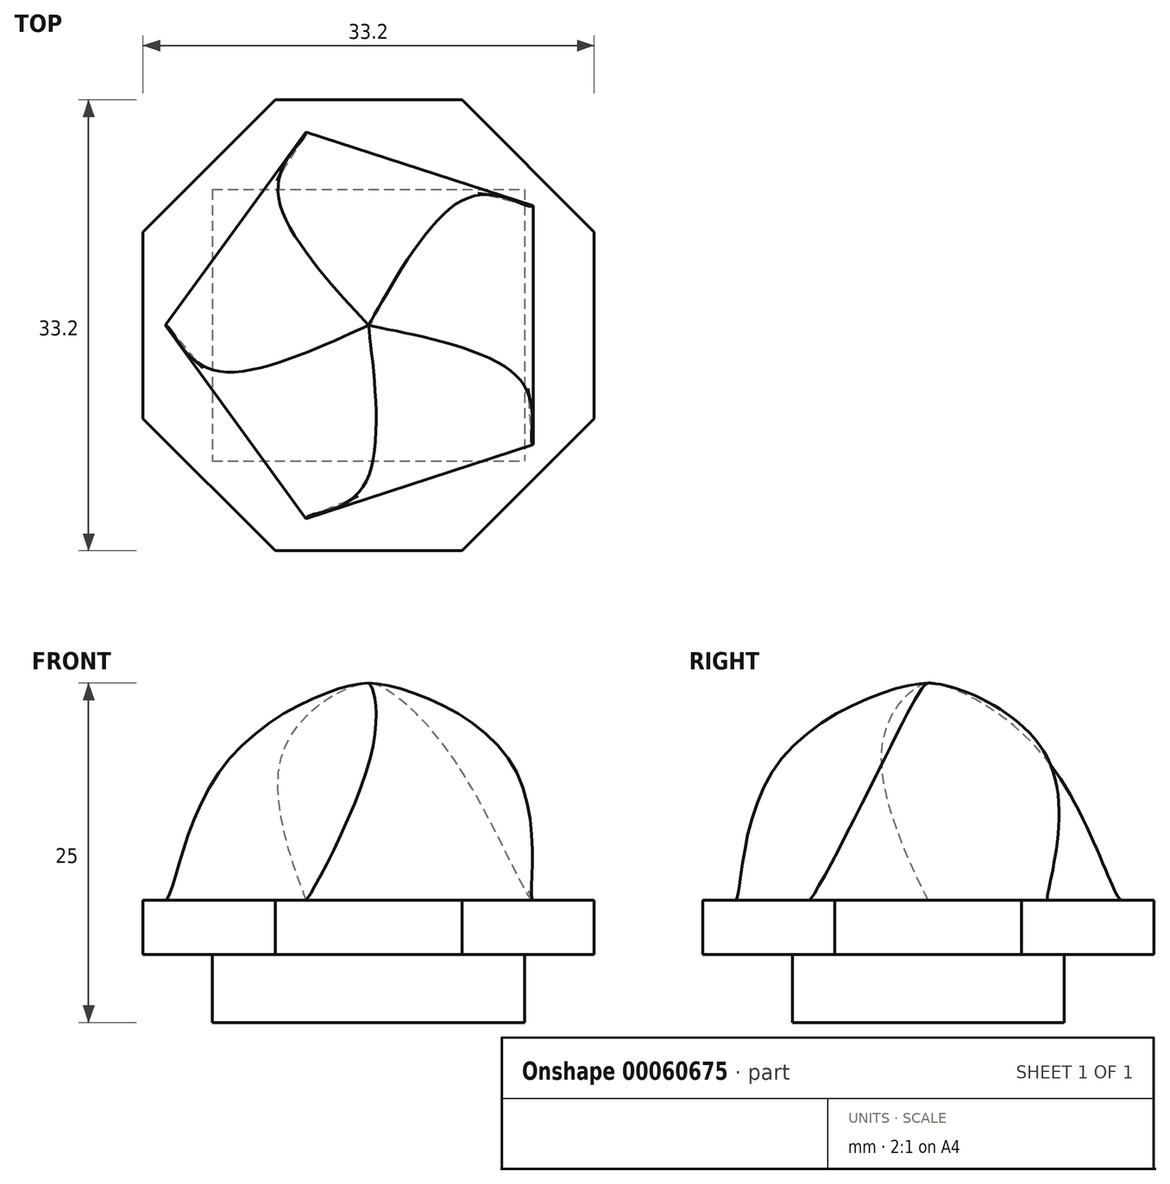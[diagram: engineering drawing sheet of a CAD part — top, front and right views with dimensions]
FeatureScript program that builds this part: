
annotation { "Feature Type Name" : "Feature", "Feature Type Description" : "" }
export const myFeature = defineFeature(function(context is Context, id is Id, definition is map)
    precondition{}
    {
        {
            var Q0;
            Q0=qCreatedBy(makeId("Top.planeOp"),FACE);
            var sketch = newSketch(context, id + "F0", { "sketchPlane" : qUnion([Q0])});
            skLineSegment(sketch, "E0.bottom", {"start": v(-11.5, 10) * mm, "end": v(11.5, 10) * mm});
            skLineSegment(sketch, "E0.top", {"start": v(-11.5, -10) * mm, "end": v(11.5, -10) * mm});
            skLineSegment(sketch, "E0.left", {"start": v(-11.5, 10) * mm, "end": v(-11.5, -10) * mm});
            skLineSegment(sketch, "E0.right", {"start": v(11.5, 10) * mm, "end": v(11.5, -10) * mm});
            skSolve(sketch);
        }
        {
            var Q0;
            Q0=qSketchRegion(id+"F0",true);
            extrude(context, id + "F1", {"entities" : qUnion([Q0]), "depth" : 5 * mm});
        }
        {
            var Q0;
            Q0=makeQuery(id+"F1.opExtrude","CAP_FACE",FACE,{"disambiguationData":[OSD([sQuery(id+"F0.wireOp",EDGE,"E0.bottom"),sQuery(id+"F0.wireOp",EDGE,"E0.top"),sQuery(id+"F0.wireOp",EDGE,"E0.left"),sQuery(id+"F0.wireOp",EDGE,"E0.right")])],"isStart":false});
            var sketch = newSketch(context, id + "F2", { "sketchPlane" : qUnion([Q0])});
            skCircle(sketch, "E1.cCircle", {"center": v(0, 0) * mm, "radius": 16.6 * mm, "construction": true});
            skLineSegment(sketch, "E1.0", {"start": v(16.6, 6.88) * mm, "end": v(16.6, -6.88) * mm});
            skLineSegment(sketch, "E1.1", {"start": v(16.6, -6.88) * mm, "end": v(6.88, -16.6) * mm});
            skLineSegment(sketch, "E1.2", {"start": v(6.88, -16.6) * mm, "end": v(-6.88, -16.6) * mm});
            skLineSegment(sketch, "E1.3", {"start": v(-6.88, -16.6) * mm, "end": v(-16.6, -6.88) * mm});
            skLineSegment(sketch, "E1.4", {"start": v(-16.6, -6.88) * mm, "end": v(-16.6, 6.88) * mm});
            skLineSegment(sketch, "E1.5", {"start": v(-16.6, 6.88) * mm, "end": v(-6.88, 16.6) * mm});
            skLineSegment(sketch, "E1.6", {"start": v(-6.88, 16.6) * mm, "end": v(6.88, 16.6) * mm});
            skLineSegment(sketch, "E1.7", {"start": v(6.88, 16.6) * mm, "end": v(16.6, 6.88) * mm});
            skPoint(sketch, "E1.0.midPoint", {"position": v(16.6, 0) * mm});
            skSolve(sketch);
        }
        {
            var Q0;
            Q0=qSketchRegion(id+"F2",true);
            extrude(context, id + "F3", {"entities" : qUnion([Q0]), "operationType" : NewBodyOperationType.ADD, "depth" : 4 * mm});
        }
        {
            var Q0;
            Q0=makeQuery(id+"F2.imprint","IMPRINT",FACE,{"disambiguationData":[TD([[makeQuery(id+"F2.imprint","IMPRINT",EDGE,{"derivedFrom":makeQuery(id+"F1.opExtrude","CAP_EDGE",EDGE,{"disambiguationData":[OSD([sQuery(id+"F0.wireOp",EDGE,"E0.bottom")])],"isStart":false})}),-1.0]])]});
            cPlane(context, id + "F4", {"entities" : qUnion([Q0]), "cplaneType" : CPlaneType.OFFSET, "offset" : 20 * mm, "width" : 150 * mm, "height" : 150 * mm});
        }
        {
            var Q0;
            Q0=qCreatedBy(id+"F4.planeOp",FACE);
            var sketch = newSketch(context, id + "F5", { "sketchPlane" : qUnion([Q0])});
            skPoint(sketch, "E2.0", {"position": v(0, 0) * mm});
            skSolve(sketch);
        }
        {
            var Q0;
            Q0=makeQuery(id+"F3.opExtrude","CAP_FACE",FACE,{"disambiguationData":[OSD([sQuery(id+"F2.wireOp",EDGE,"E1.0"),sQuery(id+"F2.wireOp",EDGE,"E1.1"),sQuery(id+"F2.wireOp",EDGE,"E1.2"),sQuery(id+"F2.wireOp",EDGE,"E1.3"),sQuery(id+"F2.wireOp",EDGE,"E1.4"),sQuery(id+"F2.wireOp",EDGE,"E1.5"),sQuery(id+"F2.wireOp",EDGE,"E1.6"),sQuery(id+"F2.wireOp",EDGE,"E1.7")])],"isStart":false});
            var sketch = newSketch(context, id + "F6", { "sketchPlane" : qUnion([Q0])});
            skPoint(sketch, "E3.0", {"position": v(0, 0) * mm});
            skCircle(sketch, "E4.cCircle", {"center": v(0, 0) * mm, "radius": 12.1 * mm, "construction": true});
            skLineSegment(sketch, "E4.0", {"start": v(12.1, 8.8) * mm, "end": v(12.1, -8.8) * mm});
            skLineSegment(sketch, "E4.1", {"start": v(12.1, -8.8) * mm, "end": v(-4.63, -14.24) * mm});
            skLineSegment(sketch, "E4.2", {"start": v(-4.63, -14.24) * mm, "end": v(-14.97, 0) * mm});
            skLineSegment(sketch, "E4.3", {"start": v(-14.97, 0) * mm, "end": v(-4.63, 14.24) * mm});
            skLineSegment(sketch, "E4.4", {"start": v(-4.63, 14.24) * mm, "end": v(12.1, 8.8) * mm});
            skPoint(sketch, "E4.0.midPoint", {"position": v(12.1, 0) * mm});
            skSolve(sketch);
        }
        {
            var Q0;
            Q0=makeQuery(id+"F6.imprint","IMPRINT",FACE,{"disambiguationData":[TD([[makeQuery(id+"F6.imprint","IMPRINT",EDGE,{"derivedFrom":sQuery(id+"F6.wireOp",EDGE,"E4.0")}),1.0]])]});
            cPlane(context, id + "F7", {"entities" : qUnion([Q0]), "cplaneType" : CPlaneType.OFFSET, "offset" : 10 * mm, "width" : 150 * mm, "height" : 150 * mm});
        }
        {
            var Q0;
            Q0=qCreatedBy(id+"F7.planeOp",FACE);
            var sketch = newSketch(context, id + "F8", { "sketchPlane" : qUnion([Q0])});
            skPoint(sketch, "E5.0", {"position": v(0, 0) * mm});
            skCircle(sketch, "E6.cCircle", {"center": v(0, 0) * mm, "radius": 9 * mm, "construction": true});
            skLineSegment(sketch, "E6.0", {"start": v(-6.54, 9) * mm, "end": v(6.54, 9) * mm});
            skLineSegment(sketch, "E6.1", {"start": v(6.54, 9) * mm, "end": v(10.58, -3.44) * mm});
            skLineSegment(sketch, "E6.2", {"start": v(10.58, -3.44) * mm, "end": v(0, -11.12) * mm});
            skLineSegment(sketch, "E6.3", {"start": v(0, -11.12) * mm, "end": v(-10.58, -3.44) * mm});
            skLineSegment(sketch, "E6.4", {"start": v(-10.58, -3.44) * mm, "end": v(-6.54, 9) * mm});
            skPoint(sketch, "E6.0.midPoint", {"position": v(0, 9) * mm});
            skSolve(sketch);
        }
        {
            var Q1;
            Q1=makeQuery(id+"F6.imprint","IMPRINT",FACE,{"disambiguationData":[TD([[makeQuery(id+"F6.imprint","IMPRINT",EDGE,{"derivedFrom":sQuery(id+"F6.wireOp",EDGE,"E4.0")}),-1.0]])]});
            var Q2;
            Q2=makeQuery(id+"F8.imprint","IMPRINT",FACE,{"disambiguationData":[TD([[makeQuery(id+"F8.imprint","IMPRINT",EDGE,{"derivedFrom":sQuery(id+"F8.wireOp",EDGE,"E6.0")}),-1.0]])]});
            var Q3;
            Q3=sQuery(id+"F5.wireOp",VERTEX,"E2.0");
            var Q4;
            Q4=sQuery(id+"F5.wireOp",VERTEX,"E2.0");
            loft(context, id + "F9", {"operationType" : NewBodyOperationType.ADD, "startCondition" : LoftEndDerivativeType.MATCH_TANGENT, "startMagnitude" : .5, "endCondition" : LoftEndDerivativeType.TANGENT_TO_PROFILE, "endMagnitude" : .5, "sheetProfilesArray" : [{ "sheetProfileEntities" : qUnion([Q1]) }, { "sheetProfileEntities" : qUnion([Q2]) }, { "sheetProfileEntities" : qUnion([Q3]) }], "connections" : [{ "connectionEntities" : qUnion([Q4]), "connectionEdgeQueries" : qUnion([]), "connectionEdgeParameters" : [] }]});
        }
    });
